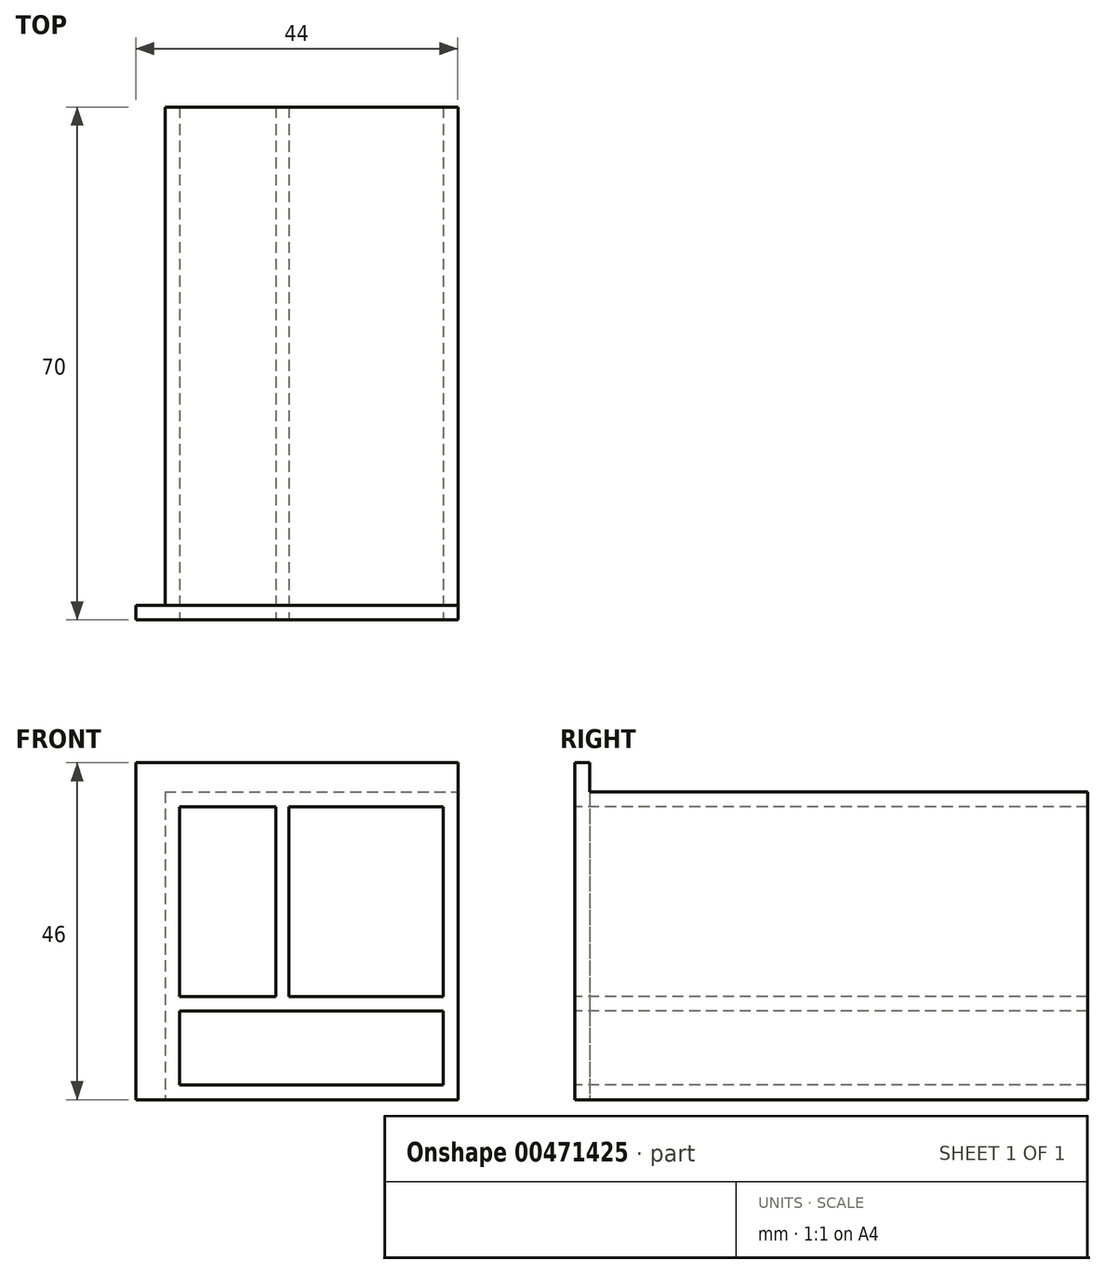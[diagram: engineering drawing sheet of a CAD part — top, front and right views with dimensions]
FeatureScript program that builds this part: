
annotation { "Feature Type Name" : "Feature", "Feature Type Description" : "" }
export const myFeature = defineFeature(function(context is Context, id is Id, definition is map)
    precondition{}
    {
        {
            var Q0;
            Q0=qCreatedBy(makeId("Front.planeOp"),FACE);
            var sketch = newSketch(context, id + "F0", { "sketchPlane" : qUnion([Q0])});
            skLineSegment(sketch, "E0.bottom", {"start": v(70.06, 58.45) * mm, "end": v(110.06, 58.45) * mm});
            skLineSegment(sketch, "E0.top", {"start": v(70.06, 16.45) * mm, "end": v(110.06, 16.45) * mm});
            skLineSegment(sketch, "E0.left", {"start": v(70.06, 58.45) * mm, "end": v(70.06, 16.45) * mm});
            skLineSegment(sketch, "E0.right", {"start": v(110.06, 58.45) * mm, "end": v(110.06, 16.45) * mm});
            skLineSegment(sketch, "E1.0", {"start": v(72.06, 56.45) * mm, "end": v(85.2, 56.45) * mm});
            skLineSegment(sketch, "E1.1", {"start": v(72.06, 56.45) * mm, "end": v(72.06, 30.51) * mm});
            skLineSegment(sketch, "E1.2", {"start": v(72.06, 18.45) * mm, "end": v(108.06, 18.45) * mm});
            skLineSegment(sketch, "E1.3", {"start": v(108.06, 56.45) * mm, "end": v(108.06, 30.51) * mm});
            skLineSegment(sketch, "E2", {"start": v(85.2, 56.45) * mm, "end": v(85.2, 30.51) * mm});
            skLineSegment(sketch, "E3", {"start": v(86.97, 56.45) * mm, "end": v(86.97, 30.51) * mm});
            skLineSegment(sketch, "E4", {"start": v(72.06, 30.51) * mm, "end": v(85.2, 30.51) * mm});
            skLineSegment(sketch, "E5", {"start": v(72.06, 28.54) * mm, "end": v(108.06, 28.54) * mm});
            skLineSegment(sketch, "E6.trimOffspring", {"start": v(86.97, 30.51) * mm, "end": v(108.06, 30.51) * mm});
            skLineSegment(sketch, "E7.trimOffspring", {"start": v(86.97, 56.45) * mm, "end": v(108.06, 56.45) * mm});
            skLineSegment(sketch, "E8.trimOffspring", {"start": v(108.06, 28.54) * mm, "end": v(108.06, 18.45) * mm});
            skLineSegment(sketch, "E9.trimOffspring", {"start": v(72.06, 28.54) * mm, "end": v(72.06, 18.45) * mm});
            skSolve(sketch);
        }
        {
            var Q0;
            Q0 = qSketchRegion(id + "F0", true);
            extrude(context, id + "F1", {"entities" : qUnion([Q0]), "oppositeDirection" : true, "depth" : 70 * mm});
        }
        {
            var Q0;
            Q0=makeQuery(id+"F1.opExtrude","CAP_FACE",FACE,{"disambiguationData":[OSD([sQuery(id+"F0.wireOp",EDGE,"E0.bottom"),sQuery(id+"F0.wireOp",EDGE,"E0.top"),sQuery(id+"F0.wireOp",EDGE,"E0.left"),sQuery(id+"F0.wireOp",EDGE,"E0.right"),sQuery(id+"F0.wireOp",EDGE,"E1.0"),sQuery(id+"F0.wireOp",EDGE,"E1.1"),sQuery(id+"F0.wireOp",EDGE,"E1.2"),sQuery(id+"F0.wireOp",EDGE,"E1.3"),sQuery(id+"F0.wireOp",EDGE,"E2"),sQuery(id+"F0.wireOp",EDGE,"E3"),sQuery(id+"F0.wireOp",EDGE,"E4"),sQuery(id+"F0.wireOp",EDGE,"E5"),sQuery(id+"F0.wireOp",EDGE,"E6.trimOffspring"),sQuery(id+"F0.wireOp",EDGE,"E7.trimOffspring"),sQuery(id+"F0.wireOp",EDGE,"E8.trimOffspring"),sQuery(id+"F0.wireOp",EDGE,"E9.trimOffspring")])],"isStart":false});
            var sketch = newSketch(context, id + "F2", { "sketchPlane" : qUnion([Q0])});
            skLineSegment(sketch, "E10.bottom", {"start": v(-110.06, 58.45) * mm, "end": v(-70.06, 58.45) * mm});
            skLineSegment(sketch, "E10.top", {"start": v(-110.06, 16.45) * mm, "end": v(-70.06, 16.45) * mm});
            skLineSegment(sketch, "E10.left", {"start": v(-110.06, 58.45) * mm, "end": v(-110.06, 16.45) * mm});
            skLineSegment(sketch, "E10.right", {"start": v(-70.06, 58.45) * mm, "end": v(-70.06, 16.45) * mm});
            skSolve(sketch);
        }
        {
            var Q0;
            Q0=makeQuery(id+"F1.opExtrude","CAP_FACE",FACE,{"disambiguationData":[OSD([sQuery(id+"F0.wireOp",EDGE,"E0.bottom"),sQuery(id+"F0.wireOp",EDGE,"E0.top"),sQuery(id+"F0.wireOp",EDGE,"E0.left"),sQuery(id+"F0.wireOp",EDGE,"E0.right"),sQuery(id+"F0.wireOp",EDGE,"E1.0"),sQuery(id+"F0.wireOp",EDGE,"E1.1"),sQuery(id+"F0.wireOp",EDGE,"E1.2"),sQuery(id+"F0.wireOp",EDGE,"E1.3"),sQuery(id+"F0.wireOp",EDGE,"E2"),sQuery(id+"F0.wireOp",EDGE,"E3"),sQuery(id+"F0.wireOp",EDGE,"E4"),sQuery(id+"F0.wireOp",EDGE,"E5"),sQuery(id+"F0.wireOp",EDGE,"E6.trimOffspring"),sQuery(id+"F0.wireOp",EDGE,"E7.trimOffspring"),sQuery(id+"F0.wireOp",EDGE,"E8.trimOffspring"),sQuery(id+"F0.wireOp",EDGE,"E9.trimOffspring")])],"isStart":true});
            var sketch = newSketch(context, id + "F3", { "sketchPlane" : qUnion([Q0])});
            skLineSegment(sketch, "E11.0", {"start": v(66.06, 62.45) * mm, "end": v(110.06, 62.45) * mm});
            skLineSegment(sketch, "E11.1", {"start": v(66.06, 62.45) * mm, "end": v(66.06, 16.45) * mm});
            skLineSegment(sketch, "E12", {"start": v(66.06, 16.45) * mm, "end": v(70.06, 16.45) * mm});
            skLineSegment(sketch, "E13", {"start": v(70.06, 16.45) * mm, "end": v(70.06, 58.45) * mm});
            skLineSegment(sketch, "E14", {"start": v(70.06, 58.45) * mm, "end": v(110.06, 58.45) * mm});
            skLineSegment(sketch, "E15", {"start": v(110.06, 58.45) * mm, "end": v(110.06, 62.45) * mm});
            skSolve(sketch);
        }
        {
            var Q0;
            Q0 = qSketchRegion(id + "F3", true);
            extrude(context, id + "F4", {"entities" : qUnion([Q0]), "operationType" : NewBodyOperationType.ADD, "oppositeDirection" : true, "depth" : 2 * mm});
        }
    });
